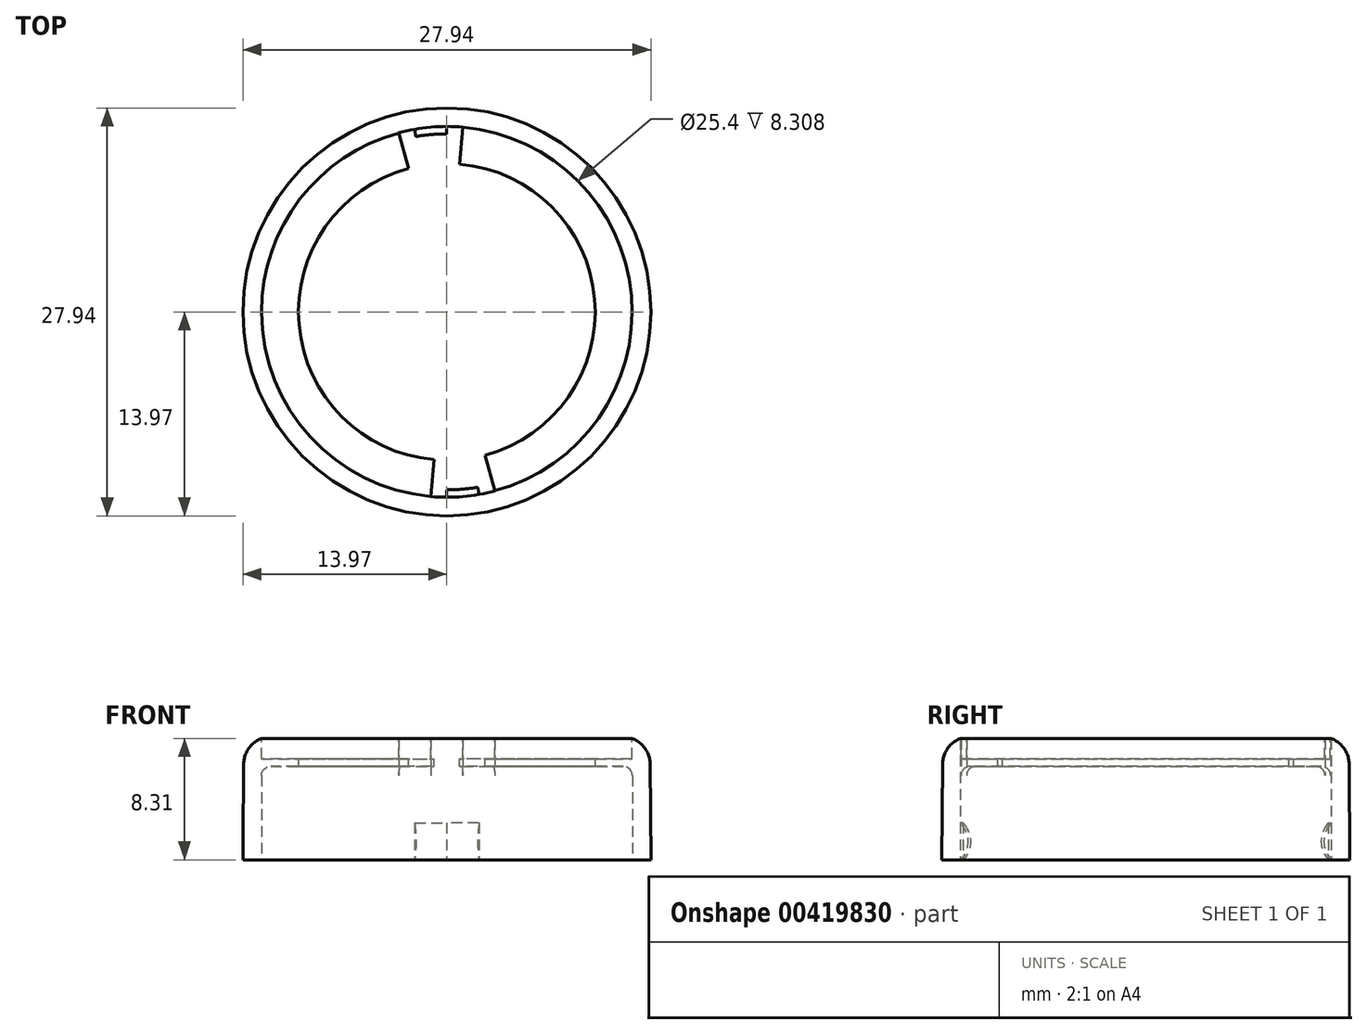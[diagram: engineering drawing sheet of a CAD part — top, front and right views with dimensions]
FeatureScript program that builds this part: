
annotation { "Feature Type Name" : "Feature", "Feature Type Description" : "" }
export const myFeature = defineFeature(function(context is Context, id is Id, definition is map)
    precondition{}
    {
        {
            var Q0;
            Q0=qCreatedBy(makeId("Front.planeOp"),FACE);
            var sketch = newSketch(context, id + "F0", { "sketchPlane" : qUnion([Q0])});
            skLineSegment(sketch, "E0", {"start": v(-12.7, 0) * mm, "end": v(-12.7, 5.77) * mm});
            skLineSegment(sketch, "E1", {"start": v(-12.07, 6.4) * mm, "end": v(0, 6.4) * mm});
            skLineSegment(sketch, "E2", {"start": v(0, 6.4) * mm, "end": v(0, 8.44) * mm});
            skLineSegment(sketch, "E3", {"start": v(0, 8.44) * mm, "end": v(-12.01, 8.44) * mm});
            skLineSegment(sketch, "E4", {"start": v(-13.97, 0) * mm, "end": v(-12.7, 0) * mm});
            skLineSegment(sketch, "E5", {"start": v(-13.92, 6.55) * mm, "end": v(-13.97, 0) * mm});
            skPoint(sketch, "E6.visualSharp", {"position": v(-13.9, 8.44) * mm});
            skArc(sketch, "E6.filletArc", {"start": v(-12.01, 8.44) * mm, "mid": v(-13.36, 7.88) * mm, "end": v(-13.92, 6.55) * mm});
            skPoint(sketch, "E7.visualSharp", {"position": v(-12.7, 6.4) * mm});
            skArc(sketch, "E7.filletArc", {"start": v(-12.07, 6.4) * mm, "mid": v(-12.51, 6.22) * mm, "end": v(-12.7, 5.77) * mm});
            skSolve(sketch);
        }
        {
            var Q0;
            Q0=makeQuery(id+"F0.imprint","IMPRINT",FACE,{"disambiguationData":[TD([[makeQuery(id+"F0.imprint","IMPRINT",EDGE,{"derivedFrom":sQuery(id+"F0.wireOp",EDGE,"E0")}),1.0]])]});
            var Q1;
            Q1=sQuery(id+"F0.wireOp",EDGE,"E2");
            revolve(context, id + "F1", {"entities" : qUnion([Q0]), "axis" : qUnion([Q1]), "revolveType" : RevolveType.FULL});
        }
        {
            var Q0;
            Q0=makeQuery(id+"F1.opRevolve","SWEPT_FACE",FACE,{"disambiguationData":[OSD([sQuery(id+"F0.wireOp",EDGE,"E3")])]});
            var sketch = newSketch(context, id + "F2", { "sketchPlane" : qUnion([Q0])});
            skCircle(sketch, "E8", {"center": v(0, 0) * mm, "radius": 12.69 * mm});
            skSolve(sketch);
        }
        {
            var Q0;
            Q0=qSketchRegion(id+"F2",true);
            extrude(context, id + "F3", {"entities" : qUnion([Q0]), "operationType" : NewBodyOperationType.REMOVE, "oppositeDirection" : true, "depth" : 1.52 * mm});
        }
        {
            var Q0;
            Q0=makeQuery(id+"F3.boolean.opBoolean","COPY",FACE,{"derivedFrom":makeQuery(id+"F3.opExtrude","CAP_FACE",FACE,{"disambiguationData":[OSD([sQuery(id+"F2.wireOp",EDGE,"E8")])],"isStart":false})});
            var sketch = newSketch(context, id + "F4", { "sketchPlane" : qUnion([Q0])});
            skCircle(sketch, "E9", {"center": v(0, 0) * mm, "radius": 10.16 * mm});
            skSolve(sketch);
        }
        {
            var Q0;
            Q0=qSketchRegion(id+"F4",true);
            extrude(context, id + "F5", {"entities" : qUnion([Q0]), "operationType" : NewBodyOperationType.REMOVE, "oppositeDirection" : true, "depth" : 25.4 * mm});
        }
        {
            var Q0;
            Q0=qCreatedBy(makeId("Right.planeOp"),FACE);
            var sketch = newSketch(context, id + "F6", { "sketchPlane" : qUnion([Q0])});
            skFitSpline(sketch, "E10", {"points": [v(-12.7, 2.54) * mm, v(-12.2, 1.27) * mm, v(-12.7, 0) * mm], "startDerivative": vector(2, -2.68) * mm, "endDerivative": vector(-2.07, -1.98) * mm});
            skFitSpline(sketch, "E11", {"points": [v(12.7, 2.54) * mm, v(12.2, 1.27) * mm, v(12.7, 0) * mm], "startDerivative": vector(-1.7, -1.76) * mm, "endDerivative": vector(1.79, -1.76) * mm});
            skLineSegment(sketch, "E12", {"start": v(0, 0) * mm, "end": v(0, 5.68) * mm});
            skLineSegment(sketch, "E13", {"start": v(-12.7, 2.54) * mm, "end": v(-12.7, 0) * mm});
            skLineSegment(sketch, "E14", {"start": v(12.7, 2.54) * mm, "end": v(12.7, 0) * mm});
            skSolve(sketch);
        }
        {
            var Q0;
            Q0=qSketchRegion(id+"F6",true);
            var Q1;
            Q1=sQuery(id+"F6.wireOp",EDGE,"E12");
            revolve(context, id + "F7", {"operationType" : NewBodyOperationType.ADD, "entities" : qUnion([Q0]), "axis" : qUnion([Q1]), "revolveType" : RevolveType.ONE_DIRECTION, "angle" : 10 * degree});
        }
        {
            var Q0;
            Q0=qCreatedBy(makeId("Right.planeOp"),FACE);
            var sketch = newSketch(context, id + "F8", { "sketchPlane" : qUnion([Q0])});
            skLineSegment(sketch, "E15.right", {"start": v(0, 5.77) * mm, "end": v(0, 8.31) * mm});
            skLineSegment(sketch, "E16.bottom", {"start": v(0, 8.31) * mm, "end": v(12.7, 8.31) * mm});
            skLineSegment(sketch, "E16.top", {"start": v(0, 5.77) * mm, "end": v(12.7, 5.77) * mm});
            skLineSegment(sketch, "E16.left", {"start": v(0, 8.31) * mm, "end": v(0, 5.77) * mm});
            skLineSegment(sketch, "E16.right", {"start": v(12.7, 8.31) * mm, "end": v(12.7, 5.77) * mm});
            skSolve(sketch);
        }
        {
            var Q0;
            Q0=makeQuery(id+"F8.imprint","IMPRINT",FACE,{"disambiguationData":[TD([[makeQuery(id+"F8.imprint","IMPRINT",EDGE,{"derivedFrom":sQuery(id+"F8.wireOp",EDGE,"E16.bottom")}),-1.0]])]});
            var Q1;
            Q1=sQuery(id+"F8.wireOp",EDGE,"E16.left");
            revolve(context, id + "F9", {"operationType" : NewBodyOperationType.REMOVE, "entities" : qUnion([Q0]), "axis" : qUnion([Q1]), "revolveType" : RevolveType.TWO_DIRECTIONS, "oppositeDirection" : true, "angle" : 15 * degree, "angleBack" : 355 * degree});
        }
        {
            var Q0;
            Q0=qCreatedBy(makeId("Right.planeOp"),FACE);
            var sketch = newSketch(context, id + "F10", { "sketchPlane" : qUnion([Q0])});
            skLineSegment(sketch, "E17.bottom", {"start": v(0, 8.31) * mm, "end": v(-12.7, 8.31) * mm});
            skLineSegment(sketch, "E17.top", {"start": v(0, 5.77) * mm, "end": v(-12.7, 5.77) * mm});
            skLineSegment(sketch, "E17.left", {"start": v(0, 8.31) * mm, "end": v(0, 5.77) * mm});
            skLineSegment(sketch, "E17.right", {"start": v(-12.7, 8.31) * mm, "end": v(-12.7, 5.77) * mm});
            skSolve(sketch);
        }
        {
            var Q0;
            Q0=qSketchRegion(id+"F10",true);
            var Q1;
            Q1=sQuery(id+"F10.wireOp",EDGE,"E17.left");
            revolve(context, id + "F11", {"operationType" : NewBodyOperationType.REMOVE, "entities" : qUnion([Q0]), "axis" : qUnion([Q1]), "revolveType" : RevolveType.TWO_DIRECTIONS, "oppositeDirection" : true, "angle" : 15 * degree, "angleBack" : 355 * degree});
        }
    });
